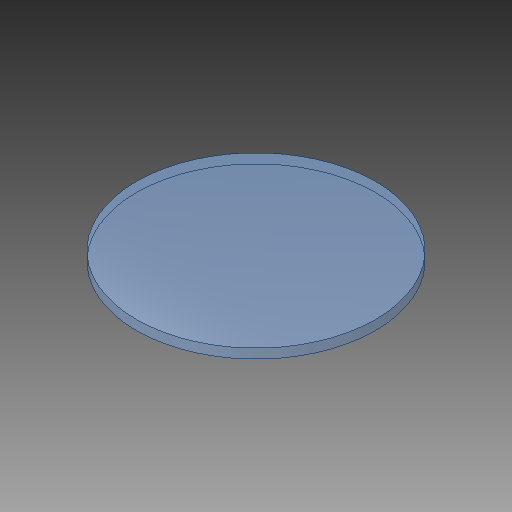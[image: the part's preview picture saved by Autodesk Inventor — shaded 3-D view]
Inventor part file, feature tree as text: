
AUTODESK INVENTOR PART (.ipt)
format: ipt  version: 2019 (Build 230136000, 136)  size: 96,768 bytes
history: native  units: in
note: dims shown in document units (in); Inventor stores cm internally (conversion verified against a paired STEP export)
features: extrude x1, sketch x1
ambient origin geometry x8: Origin, YZ Plane, XZ Plane, XY Plane, X Axis, Y Axis, Z Axis, Center Point
bodies: Solid1 (feature_tree)
feature tree (2):
  extrude  "Extrusion1"  Depth=0.0394in TaperAngle=0.0deg
  sketch  "Sketch1"  dims[d0=0.9843in d1=0.0394in d2=0.0in]
